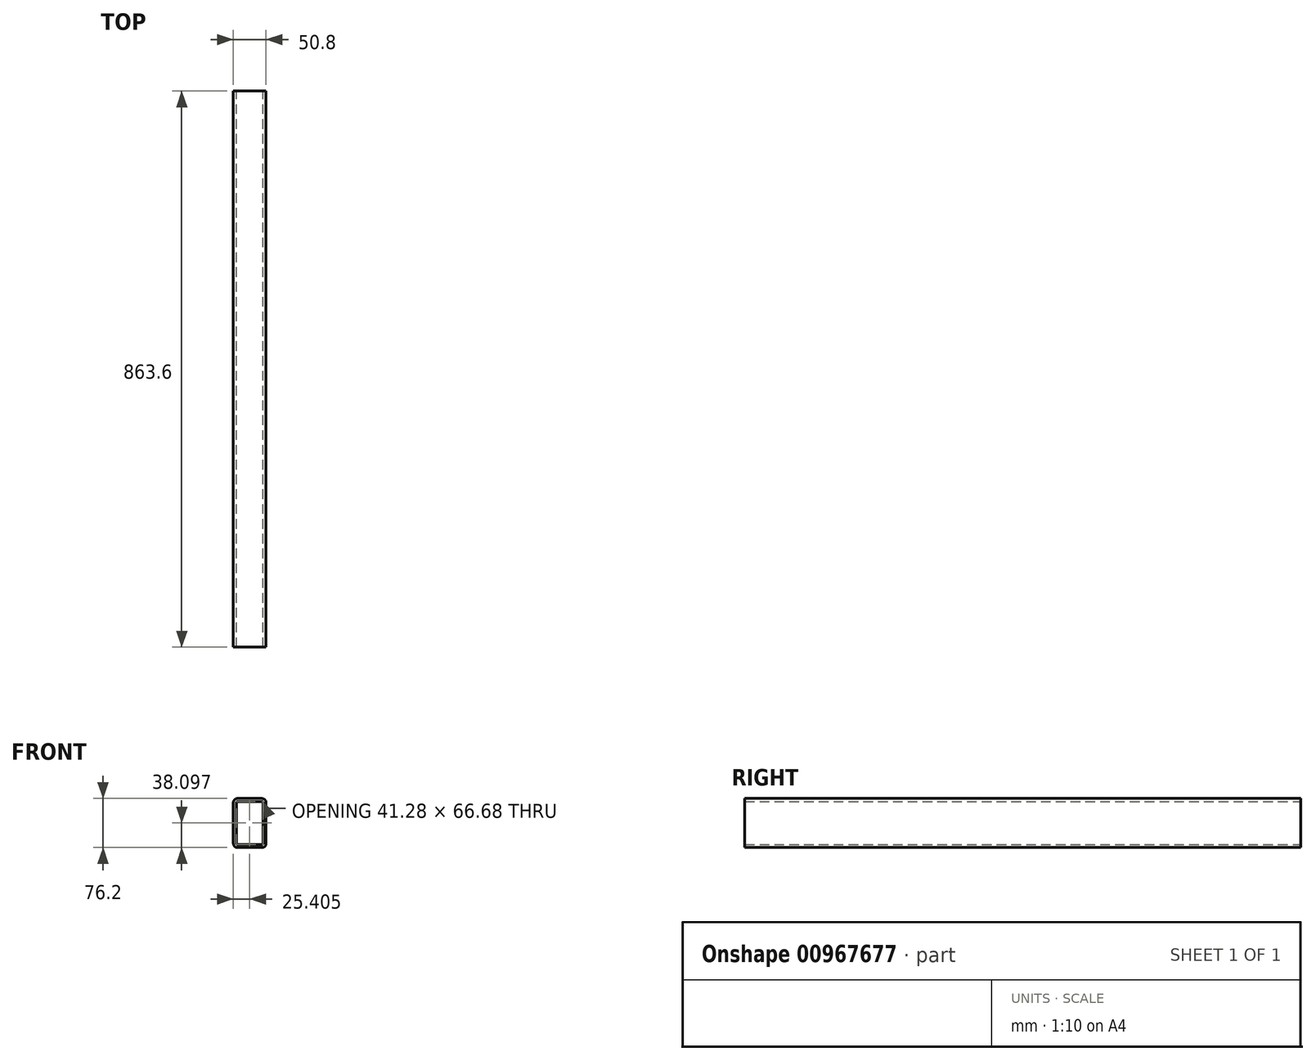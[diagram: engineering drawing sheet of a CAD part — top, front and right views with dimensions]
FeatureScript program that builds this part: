
annotation { "Feature Type Name" : "Feature", "Feature Type Description" : "" }
export const myFeature = defineFeature(function(context is Context, id is Id, definition is map)
    precondition{}
    {
        {
            var Q0;
            Q0=qCreatedBy(makeId("Front.planeOp"),FACE);
            var sketch = newSketch(context, id + "F0", { "sketchPlane" : qUnion([Q0])});
            skLineSegment(sketch, "E0.bottom", {"start": v(-71.45, 19.86) * mm, "end": v(-33.35, 19.86) * mm});
            skLineSegment(sketch, "E0.top", {"start": v(-71.45, 96.06) * mm, "end": v(-33.35, 96.06) * mm});
            skLineSegment(sketch, "E0.left", {"start": v(-77.8, 26.2) * mm, "end": v(-77.8, 89.7) * mm});
            skLineSegment(sketch, "E0.right", {"start": v(-27, 26.2) * mm, "end": v(-27, 89.7) * mm});
            skPoint(sketch, "E1.visualSharp", {"position": v(-77.8, 96.06) * mm});
            skArc(sketch, "E1.filletArc", {"start": v(-71.45, 96.06) * mm, "mid": v(-75.94, 94.2) * mm, "end": v(-77.8, 89.7) * mm});
            skPoint(sketch, "E2.visualSharp", {"position": v(-27, 96.06) * mm});
            skArc(sketch, "E2.filletArc", {"start": v(-27, 89.7) * mm, "mid": v(-28.86, 94.2) * mm, "end": v(-33.35, 96.06) * mm});
            skPoint(sketch, "E3.visualSharp", {"position": v(-27, 19.86) * mm});
            skArc(sketch, "E3.filletArc", {"start": v(-33.35, 19.86) * mm, "mid": v(-28.86, 21.72) * mm, "end": v(-27, 26.2) * mm});
            skPoint(sketch, "E4.visualSharp", {"position": v(-77.8, 19.86) * mm});
            skArc(sketch, "E4.filletArc", {"start": v(-77.8, 26.2) * mm, "mid": v(-75.94, 21.72) * mm, "end": v(-71.45, 19.86) * mm});
            skArc(sketch, "E5.0", {"start": v(-71.45, 91.3) * mm, "mid": v(-72.57, 90.83) * mm, "end": v(-73.03, 89.7) * mm});
            skLineSegment(sketch, "E5.1", {"start": v(-73.03, 26.2) * mm, "end": v(-73.03, 89.7) * mm});
            skLineSegment(sketch, "E5.2", {"start": v(-71.45, 91.3) * mm, "end": v(-33.35, 91.3) * mm});
            skArc(sketch, "E5.3", {"start": v(-73.03, 26.2) * mm, "mid": v(-72.57, 25.08) * mm, "end": v(-71.45, 24.62) * mm});
            skArc(sketch, "E5.4", {"start": v(-31.76, 89.7) * mm, "mid": v(-32.22, 90.83) * mm, "end": v(-33.35, 91.3) * mm});
            skLineSegment(sketch, "E5.5", {"start": v(-31.76, 26.2) * mm, "end": v(-31.76, 89.7) * mm});
            skArc(sketch, "E5.6", {"start": v(-33.35, 24.62) * mm, "mid": v(-32.22, 25.08) * mm, "end": v(-31.76, 26.2) * mm});
            skLineSegment(sketch, "E5.7", {"start": v(-71.45, 24.62) * mm, "end": v(-33.35, 24.62) * mm});
            skSolve(sketch);
        }
        {
            var Q0;
            Q0 = qSketchRegion(id + "F0", true);
            extrude(context, id + "F1", {"entities" : qUnion([Q0]), "depth" : 863.6 * mm, "offsetDistance" : 25.4 * mm});
        }
    });
